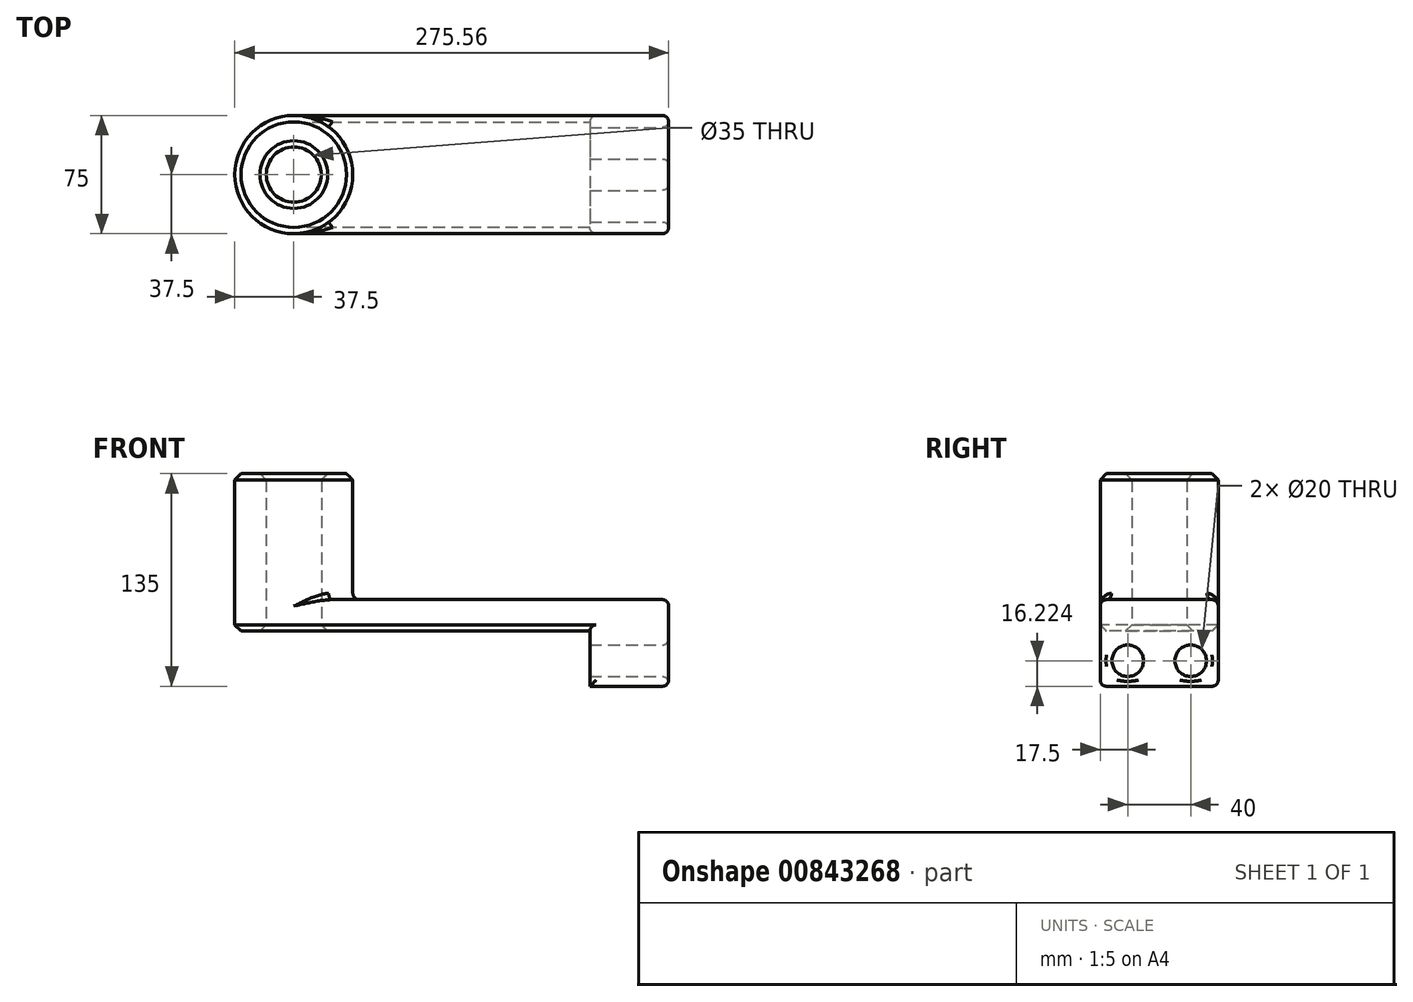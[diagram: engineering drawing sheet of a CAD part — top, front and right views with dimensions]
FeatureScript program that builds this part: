
annotation { "Feature Type Name" : "Feature", "Feature Type Description" : "" }
export const myFeature = defineFeature(function(context is Context, id is Id, definition is map)
    precondition{}
    {
        {
            var Q0;
            Q0=qCreatedBy(makeId("Top.planeOp"),FACE);
            var sketch = newSketch(context, id + "F0", { "sketchPlane" : qUnion([Q0])});
            skLineSegment(sketch, "E0.bottom", {"start": v(119.03, 37.5) * mm, "end": v(-119.03, 37.5) * mm});
            skLineSegment(sketch, "E0.top", {"start": v(119.03, -37.5) * mm, "end": v(-119.03, -37.5) * mm});
            skLineSegment(sketch, "E0.left", {"start": v(119.03, 37.5) * mm, "end": v(119.03, -37.5) * mm});
            skLineSegment(sketch, "E0.right", {"start": v(-119.03, 37.5) * mm, "end": v(-119.03, -37.5) * mm});
            skPoint(sketch, "E0.middle", {"position": v(0, 0) * mm});
            skCircle(sketch, "E1", {"center": v(-119.03, 0) * mm, "radius": 37.5 * mm});
            skCircle(sketch, "E2", {"center": v(-119.03, 0) * mm, "radius": 17.5 * mm});
            skSolve(sketch);
        }
        {
            var Q0;
            Q0 = qSketchRegion(id + "F0", true);
            extrude(context, id + "F1", {"entities" : qUnion([Q0]), "depth" : 20 * mm, "offsetDistance" : 25 * mm});
        }
        {
            var Q0;
            {var subQ1=sQuery(id+"F0.wireOp",EDGE,"E0.right");var subQ3=sQuery(id+"F0.wireOp",EDGE,"E2");var subQ4=makeQuery(id+"F0.imprint","INTERSECT",VERTEX,{"disambiguationData":[OD(0.0)],"derivedFrom":[subQ1,subQ3]});Q0=makeQuery(id+"F0.imprint","IMPRINT",FACE,{"disambiguationData":[TD([[makeQuery(id+"F0.imprint","IMPRINT",EDGE,{"disambiguationData":[TD([[subQ4,1.0]])],"derivedFrom":subQ3}),-1.0]])]});}
            var Q1;
            {var subQ1=sQuery(id+"F0.wireOp",EDGE,"E0.right");var subQ3=sQuery(id+"F0.wireOp",EDGE,"E2");var subQ4=makeQuery(id+"F0.imprint","INTERSECT",VERTEX,{"disambiguationData":[OD(0.0)],"derivedFrom":[subQ1,subQ3]});Q1=makeQuery(id+"F0.imprint","IMPRINT",FACE,{"disambiguationData":[TD([[makeQuery(id+"F0.imprint","IMPRINT",EDGE,{"disambiguationData":[TD([[subQ4,-1.0]])],"derivedFrom":subQ3}),-1.0]])]});}
            extrude(context, id + "F2", {"entities" : qUnion([Q0, Q1]), "operationType" : NewBodyOperationType.ADD, "depth" : 100 * mm, "offsetDistance" : 25 * mm});
        }
        {
            var Q0;
            Q0=makeQuery(id+"F1.opExtrude","SWEPT_FACE",FACE,{"disambiguationData":[OSD([sQuery(id+"F0.wireOp",EDGE,"E0.left")])]});
            var sketch = newSketch(context, id + "F3", { "sketchPlane" : qUnion([Q0])});
            skLineSegment(sketch, "E3.bottom", {"start": v(-37.5, 20) * mm, "end": v(37.5, 20) * mm});
            skLineSegment(sketch, "E3.top", {"start": v(-37.5, -35) * mm, "end": v(37.5, -35) * mm});
            skLineSegment(sketch, "E3.left", {"start": v(-37.5, 20) * mm, "end": v(-37.5, -35) * mm});
            skLineSegment(sketch, "E3.right", {"start": v(37.5, 20) * mm, "end": v(37.5, -35) * mm});
            skCircle(sketch, "E4", {"center": v(-20, -18.78) * mm, "radius": 10 * mm});
            skLineSegment(sketch, "E5", {"start": v(0, 0) * mm, "end": v(0, -35) * mm, "construction": true});
            skCircle(sketch, "E6.MirrorC", {"center": v(20, -18.78) * mm, "radius": 10 * mm});
            skSolve(sketch);
        }
        {
            var Q0;
            {var subQ2=sQuery(id+"F3.wireOp",EDGE,"E3.top");Q0=makeQuery(id+"F3.imprint","IMPRINT",FACE,{"disambiguationData":[TD([[makeQuery(id+"F3.imprint","IMPRINT",EDGE,{"derivedFrom":subQ2}),1.0]])]});}
            extrude(context, id + "F4", {"entities" : qUnion([Q0]), "operationType" : NewBodyOperationType.ADD, "oppositeDirection" : true, "depth" : 50 * mm, "offsetDistance" : 25 * mm});
        }
        {
            var Q0;
            Q0=makeQuery(id+"F1.opExtrude","CAP_EDGE",EDGE,{"disambiguationData":[OSD([sQuery(id+"F0.wireOp",EDGE,"E0.top")])],"isStart":false});
            var Q1;
            {var subQ0=sQuery(id+"F0.wireOp",EDGE,"E1");Q1=makeQuery(id+"F2.boolean.opBoolean","INTERSECT",EDGE,{"derivedFrom":[makeQuery(id+"F1.opExtrude","CAP_FACE",FACE,{"disambiguationData":[OSD([sQuery(id+"F0.wireOp",EDGE,"E0.bottom"),sQuery(id+"F0.wireOp",EDGE,"E0.top"),sQuery(id+"F0.wireOp",EDGE,"E0.left"),subQ0,sQuery(id+"F0.wireOp",EDGE,"E2")])],"isStart":false}),makeQuery(id+"F2.opExtrude","SWEPT_FACE",FACE,{"disambiguationData":[OSD([subQ0])]})]});}
            var Q2;
            Q2=makeQuery(id+"F1.opExtrude","CAP_EDGE",EDGE,{"disambiguationData":[OSD([sQuery(id+"F0.wireOp",EDGE,"E0.bottom")])],"isStart":false});
            var Q3;
            Q3=makeQuery(id+"F4.opExtrude","CAP_EDGE",EDGE,{"disambiguationData":[OSD([sQuery(id+"F3.wireOp",EDGE,"E3.left")])],"isStart":false});
            var Q4;
            Q4=makeQuery(id+"F4.opExtrude","SWEPT_EDGE",EDGE,{"disambiguationData":[OSD([sQuery(id+"F3.wireOp",EDGE,"E3.top"),sQuery(id+"F3.wireOp",EDGE,"E3.left")])]});
            var Q5;
            Q5=makeQuery(id+"F4.opExtrude","CAP_EDGE",EDGE,{"disambiguationData":[OSD([sQuery(id+"F3.wireOp",EDGE,"E3.right")])],"isStart":false});
            var Q6;
            Q6=makeQuery(id+"F4.opExtrude","SWEPT_EDGE",EDGE,{"disambiguationData":[OSD([sQuery(id+"F3.wireOp",EDGE,"E3.top"),sQuery(id+"F3.wireOp",EDGE,"E3.right")])]});
            var Q7;
            {var subQ0=sQuery(id+"F0.wireOp",EDGE,"E0.left");Q7=makeQuery(id+"F4.boolean.opBoolean","MERGE",FACE,{"derivedFrom":[makeQuery(id+"F1.opExtrude","SWEPT_FACE",FACE,{"disambiguationData":[OSD([subQ0])]}),makeQuery(id+"F4.opExtrude","CAP_FACE",FACE,{"disambiguationData":[OSD([subQ0,sQuery(id+"F3.wireOp",EDGE,"E3.top"),sQuery(id+"F3.wireOp",EDGE,"E3.left"),sQuery(id+"F3.wireOp",EDGE,"E3.right"),sQuery(id+"F3.wireOp",EDGE,"E6.MirrorC"),sQuery(id+"F3.wireOp",EDGE,"E4")])],"isStart":true})]});}
            fillet(context, id + "F5", {"entities" : qUnion([Q0, Q1, Q2, Q3, Q4, Q5, Q6, Q7]), "radius" : 4 * mm, "tangentPropagation" : true, "allowEdgeOverflow" : false});
        }
        {
            var Q0;
            {var subQ0=sQuery(id+"F0.wireOp",EDGE,"E2");Q0=makeQuery(id+"F2.boolean.opBoolean","MERGE",FACE,{"derivedFrom":[makeQuery(id+"F1.opExtrude","SWEPT_FACE",FACE,{"disambiguationData":[OSD([subQ0])]}),makeQuery(id+"F2.opExtrude","SWEPT_FACE",FACE,{"disambiguationData":[OSD([subQ0])]})]});}
            var Q1;
            Q1=makeQuery(id+"F2.opExtrude","CAP_EDGE",EDGE,{"disambiguationData":[OSD([sQuery(id+"F0.wireOp",EDGE,"E1")])],"isStart":false});
            var Q2;
            Q2=makeQuery(id+"F1.opExtrude","CAP_EDGE",EDGE,{"disambiguationData":[OSD([sQuery(id+"F0.wireOp",EDGE,"E1")])],"isStart":true});
            chamfer(context, id + "F6", {"entities" : qUnion([Q0, Q1, Q2]), "width" : 4 * mm, "tangentPropagation" : true});
        }
    });
